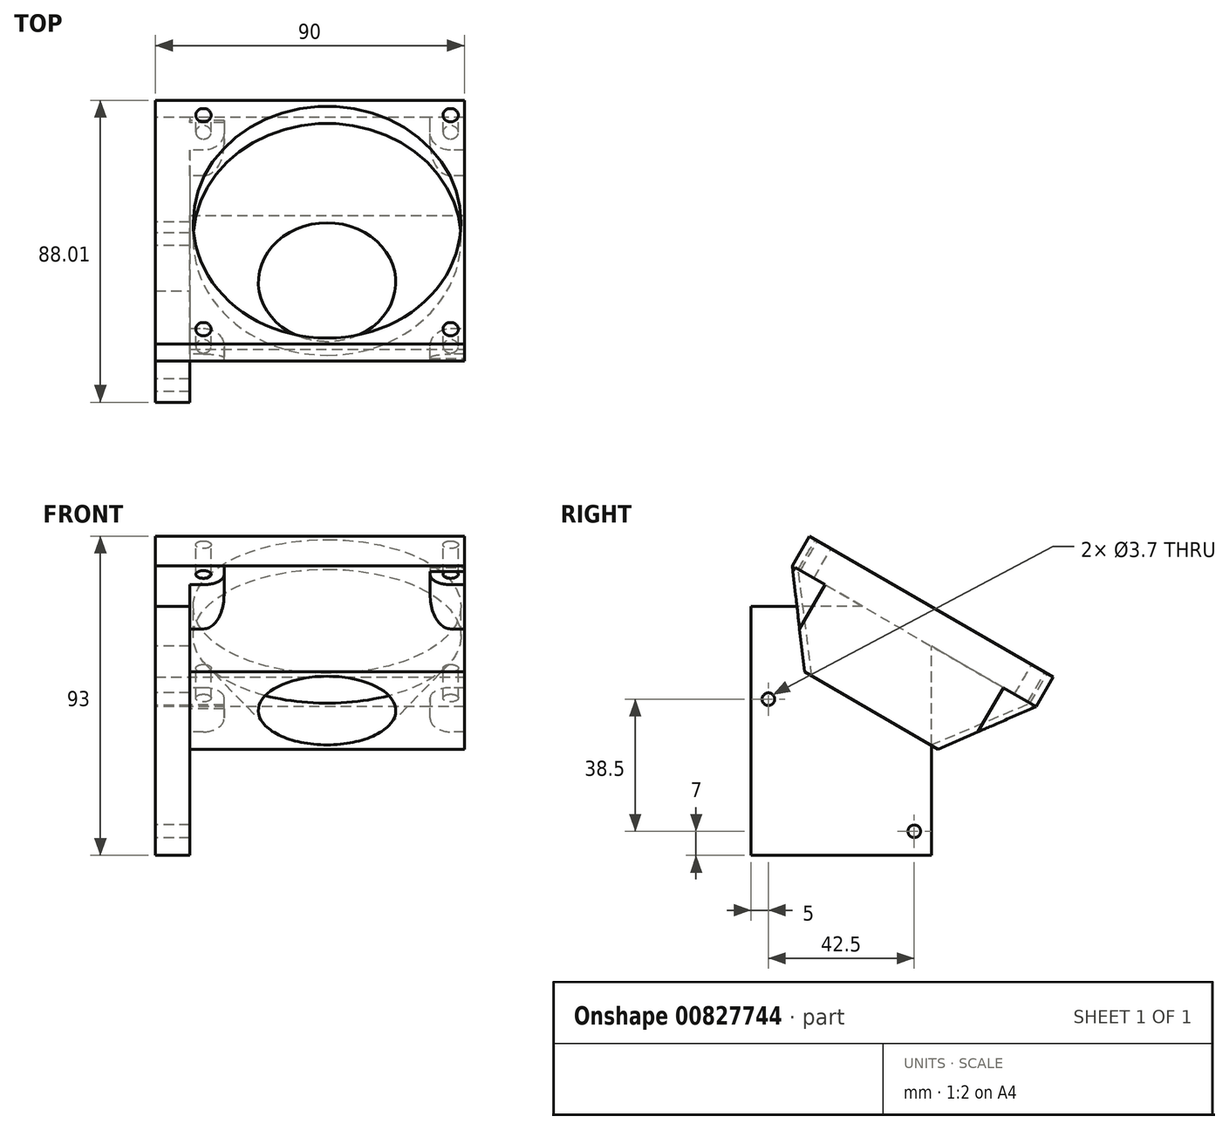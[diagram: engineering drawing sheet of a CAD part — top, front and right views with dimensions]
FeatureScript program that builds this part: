
annotation { "Feature Type Name" : "Feature", "Feature Type Description" : "" }
export const myFeature = defineFeature(function(context is Context, id is Id, definition is map)
    precondition{}
    {
        {
            var Q0;
            Q0=qCreatedBy(makeId("Right.planeOp"),FACE);
            var sketch = newSketch(context, id + "F0", { "sketchPlane" : qUnion([Q0])});
            skCircle(sketch, "E0", {"center": v(21.25, 7) * mm, "radius": 1.85 * mm});
            skCircle(sketch, "E1", {"center": v(-21.25, 45.5) * mm, "radius": 1.85 * mm});
            skLineSegment(sketch, "E2", {"start": v(26.25, 0) * mm, "end": v(-26.25, 0) * mm});
            skLineSegment(sketch, "E3", {"start": v(-26.25, 72.5) * mm, "end": v(-26.25, 0) * mm});
            skLineSegment(sketch, "E4", {"start": v(26.25, 0) * mm, "end": v(26.25, 72.5) * mm});
            skLineSegment(sketch, "E5", {"start": v(26.25, 72.5) * mm, "end": v(-26.25, 72.5) * mm});
            skLineSegment(sketch, "E6", {"start": v(0, -20.83) * mm, "end": v(0, 71.54) * mm, "construction": true});
            skLineSegment(sketch, "E7", {"start": v(-21.25, 45.5) * mm, "end": v(-21.25, 71.19) * mm, "construction": true});
            skLineSegment(sketch, "E8", {"start": v(21.25, 7) * mm, "end": v(21.25, 71.54) * mm, "construction": true});
            skSolve(sketch);
        }
        {
            var Q0;
            Q0=qSketchRegion(id+"F0",true);
            extrude(context, id + "F1", {"entities" : qUnion([Q0]), "depth" : 10 * mm, "offsetDistance" : 25 * mm});
        }
        {
            var Q0;
            Q0=qCreatedBy(makeId("Front.planeOp"),FACE);
            var Q1;
            Q1=makeQuery(id+"F1.opExtrude","SWEPT_EDGE",EDGE,{"disambiguationData":[OSD([sQuery(id+"F0.wireOp",EDGE,"E4"),sQuery(id+"F0.wireOp",EDGE,"E5")])]});
            cPlane(context, id + "F2", {"entities" : qUnion([Q0, Q1]), "cplaneType" : CPlaneType.LINE_ANGLE, "offset" : 25 * mm, "angle" : 30 * degree, "width" : 150 * mm, "height" : 150 * mm});
        }
        {
            var Q0;
            Q0=qCreatedBy(id+"F2.planeOp",FACE);
            var sketch = newSketch(context, id + "F3", { "sketchPlane" : qUnion([Q0])});
            skLineSegment(sketch, "E9", {"start": v(-90, 75.91) * mm, "end": v(-90, 65.91) * mm});
            skLineSegment(sketch, "E10", {"start": v(-90, 65.91) * mm, "end": v(0, 65.91) * mm});
            skLineSegment(sketch, "E11", {"start": v(0, 65.91) * mm, "end": v(0, 75.91) * mm});
            skLineSegment(sketch, "E12", {"start": v(0, 75.91) * mm, "end": v(-90, 75.91) * mm});
            skSolve(sketch);
        }
        {
            var Q0;
            Q0=qSketchRegion(id+"F3",true);
            extrude(context, id + "F4", {"entities" : qUnion([Q0]), "operationType" : NewBodyOperationType.ADD, "endBound" : BoundingType.SYMMETRIC, "depth" : 82 * mm, "offsetDistance" : 25 * mm});
        }
        {
            var Q0;
            Q0=makeQuery(id+"F4.opExtrude","SWEPT_FACE",FACE,{"disambiguationData":[OSD([sQuery(id+"F3.wireOp",EDGE,"E12")])]});
            var sketch = newSketch(context, id + "F5", { "sketchPlane" : qUnion([Q0])});
            skLineSegment(sketch, "E13.bottom", {"start": v(86, -49.52) * mm, "end": v(14, -49.52) * mm, "construction": true});
            skLineSegment(sketch, "E13.top", {"start": v(86, 22.48) * mm, "end": v(14, 22.48) * mm, "construction": true});
            skLineSegment(sketch, "E13.left", {"start": v(86, -49.52) * mm, "end": v(86, 22.48) * mm, "construction": true});
            skLineSegment(sketch, "E13.right", {"start": v(14, -49.52) * mm, "end": v(14, 22.48) * mm, "construction": true});
            skPoint(sketch, "E13.middle", {"position": v(50, -13.52) * mm});
            skCircle(sketch, "E14", {"center": v(14, -49.52) * mm, "radius": 2.25 * mm});
            skCircle(sketch, "E15", {"center": v(86, -49.52) * mm, "radius": 2.25 * mm});
            skCircle(sketch, "E16", {"center": v(86, 22.48) * mm, "radius": 2.25 * mm});
            skCircle(sketch, "E17", {"center": v(14, 22.48) * mm, "radius": 2.25 * mm});
            skCircle(sketch, "E18", {"center": v(50, -13.52) * mm, "radius": 39 * mm});
            skLineSegment(sketch, "E19", {"start": v(0, -13.52) * mm, "end": v(90, -13.52) * mm, "construction": true});
            skLineSegment(sketch, "E20", {"start": v(50, -13.52) * mm, "end": v(50, -90.47) * mm, "construction": true});
            skSolve(sketch);
        }
        {
            var Q0;
            Q0=makeQuery(id+"F4.opExtrude","SWEPT_FACE",FACE,{"disambiguationData":[OSD([sQuery(id+"F3.wireOp",EDGE,"E10")])]});
            cPlane(context, id + "F6", {"entities" : qUnion([Q0]), "cplaneType" : CPlaneType.OFFSET, "offset" : 25 * mm, "width" : 150 * mm, "height" : 150 * mm});
        }
        {
            var Q0;
            Q0=qSketchRegion(id+"F5",true);
            extrude(context, id + "F7", {"entities" : qUnion([Q0]), "operationType" : NewBodyOperationType.REMOVE, "endBound" : BoundingType.THROUGH_ALL, "oppositeDirection" : true, "depth" : 25 * mm, "offsetDistance" : 25 * mm});
        }
        {
            var Q0;
            Q0=qCreatedBy(id+"F6.planeOp",FACE);
            var sketch = newSketch(context, id + "F8", { "sketchPlane" : qUnion([Q0])});
            skPoint(sketch, "E21", {"position": v(50, 13.52) * mm});
            skLineSegment(sketch, "E22.bottom", {"start": v(10, 36.02) * mm, "end": v(90, 36.02) * mm});
            skLineSegment(sketch, "E22.top", {"start": v(10, -8.98) * mm, "end": v(90, -8.98) * mm});
            skLineSegment(sketch, "E22.left", {"start": v(10, 36.02) * mm, "end": v(10, -8.98) * mm});
            skLineSegment(sketch, "E22.right", {"start": v(90, 36.02) * mm, "end": v(90, -8.98) * mm});
            skLineSegment(sketch, "E23", {"start": v(50, 13.52) * mm, "end": v(-9.33, 13.52) * mm, "construction": true});
            skSolve(sketch);
        }
        {
            var Q0;
            Q0=makeQuery(id+"F4.opExtrude","SWEPT_FACE",FACE,{"disambiguationData":[OSD([sQuery(id+"F3.wireOp",EDGE,"E10")])]});
            var sketch = newSketch(context, id + "F9", { "sketchPlane" : qUnion([Q0])});
            skLineSegment(sketch, "E24.0", {"start": v(90, 54.52) * mm, "end": v(10, 54.52) * mm});
            skLineSegment(sketch, "E24.1", {"start": v(90, -27.48) * mm, "end": v(90, 54.52) * mm});
            skLineSegment(sketch, "E24.2", {"start": v(90, -27.48) * mm, "end": v(10, -27.48) * mm});
            skLineSegment(sketch, "E25", {"start": v(10, -27.48) * mm, "end": v(10, 54.52) * mm});
            skSolve(sketch);
        }
        {
            var Q1;
            Q1 = qSketchRegion(id + "F9", true);
            var Q2;
            Q2 = qSketchRegion(id + "F8", true);
            var Q3;
            Q3=sQuery(id+"F9.wireOp",VERTEX,"E24.0.end");
            var Q4;
            Q4=sQuery(id+"F8.wireOp",VERTEX,"E22.bottom.start");
            loft(context, id + "F10", {"operationType" : NewBodyOperationType.ADD, "sheetProfilesArray" : [{ "sheetProfileEntities" : qUnion([Q1]) }, { "sheetProfileEntities" : qUnion([Q2]) }], "matchConnections" : true, "connections" : [{ "connectionEntities" : qUnion([Q3, Q4]), "connectionEdgeQueries" : qUnion([]), "connectionEdgeParameters" : [] }]});
        }
        {
            var Q0;
            Q0=makeQuery(id+"F9.imprint","IMPRINT",FACE,{"disambiguationData":[TD([[makeQuery(id+"F9.imprint","IMPRINT",EDGE,{"derivedFrom":makeQuery(id+"F7.boolean.opBoolean","INTERSECT",EDGE,{"derivedFrom":[makeQuery(id+"F4.opExtrude","SWEPT_FACE",FACE,{"disambiguationData":[OSD([sQuery(id+"F3.wireOp",EDGE,"E10")])]}),makeQuery(id+"F7.opExtrude","SWEPT_FACE",FACE,{"disambiguationData":[OSD([sQuery(id+"F5.wireOp",EDGE,"E18")])]})]})}),1.0]])]});
            var sketch = newSketch(context, id + "F11", { "sketchPlane" : qUnion([Q0])});
            skCircle(sketch, "E26.0", {"center": v(50, 13.52) * mm, "radius": 39 * mm});
            skSolve(sketch);
        }
        {
            var Q0;
            Q0=makeQuery(id+"F10.opLoft","CAP_FACE",FACE,{"disambiguationData":[OSD([makeQuery(id+"F8.imprint","IMPRINT",FACE,{"disambiguationData":[TD([[makeQuery(id+"F8.imprint","IMPRINT",EDGE,{"derivedFrom":sQuery(id+"F8.wireOp",EDGE,"E22.bottom")}),-1.0]])]})])],"isStart":true});
            var sketch = newSketch(context, id + "F12", { "sketchPlane" : qUnion([Q0])});
            skCircle(sketch, "E27", {"center": v(50, 13.52) * mm, "radius": 20 * mm});
            skSolve(sketch);
        }
        {
            var Q1;
            Q1 = qSketchRegion(id + "F11", true);
            var Q2;
            Q2 = qSketchRegion(id + "F12", true);
            loft(context, id + "F13", {"operationType" : NewBodyOperationType.REMOVE, "sheetProfilesArray" : [{ "sheetProfileEntities" : qUnion([Q1]) }, { "sheetProfileEntities" : qUnion([Q2]) }]});
        }
        {
            var Q0;
            Q0=makeQuery(id+"F4.opExtrude","SWEPT_FACE",FACE,{"disambiguationData":[OSD([sQuery(id+"F3.wireOp",EDGE,"E10")])]});
            var sketch = newSketch(context, id + "F14", { "sketchPlane" : qUnion([Q0])});
            skArc(sketch, "E28", {"start": v(14, 43.52) * mm, "mid": v(18.24, 45.27) * mm, "end": v(20, 49.52) * mm});
            skLineSegment(sketch, "E29", {"start": v(20, 49.52) * mm, "end": v(20, 54.52) * mm});
            skLineSegment(sketch, "E30", {"start": v(10, 43.52) * mm, "end": v(14, 43.52) * mm});
            skLineSegment(sketch, "E31", {"start": v(10, 43.52) * mm, "end": v(10, 54.52) * mm});
            skLineSegment(sketch, "E32", {"start": v(10, 54.52) * mm, "end": v(20, 54.52) * mm});
            skLineSegment(sketch, "E33.1.0", {"start": v(20, -26.48) * mm, "end": v(9, -26.48) * mm});
            skLineSegment(sketch, "E33.1.1", {"start": v(14, -16.48) * mm, "end": v(9, -16.48) * mm});
            skLineSegment(sketch, "E33.1.2", {"start": v(20, -26.48) * mm, "end": v(20, -22.48) * mm});
            skArc(sketch, "E33.1.3", {"start": v(20, -22.48) * mm, "mid": v(18.24, -18.24) * mm, "end": v(14, -16.48) * mm});
            skLineSegment(sketch, "E33.1.4", {"start": v(9, -26.48) * mm, "end": v(9, -16.48) * mm});
            skLineSegment(sketch, "E33.2.0", {"start": v(90, -16.48) * mm, "end": v(90, -27.48) * mm});
            skLineSegment(sketch, "E33.2.1", {"start": v(80, -22.48) * mm, "end": v(80, -27.48) * mm});
            skLineSegment(sketch, "E33.2.2", {"start": v(90, -16.48) * mm, "end": v(86, -16.48) * mm});
            skArc(sketch, "E33.2.3", {"start": v(86, -16.48) * mm, "mid": v(81.76, -18.24) * mm, "end": v(80, -22.48) * mm});
            skLineSegment(sketch, "E33.2.4", {"start": v(90, -27.48) * mm, "end": v(80, -27.48) * mm});
            skLineSegment(sketch, "E33.3.0", {"start": v(80, 53.52) * mm, "end": v(91, 53.52) * mm});
            skLineSegment(sketch, "E33.3.1", {"start": v(86, 43.52) * mm, "end": v(91, 43.52) * mm});
            skLineSegment(sketch, "E33.3.2", {"start": v(80, 53.52) * mm, "end": v(80, 49.52) * mm});
            skArc(sketch, "E33.3.3", {"start": v(80, 49.52) * mm, "mid": v(81.76, 45.27) * mm, "end": v(86, 43.52) * mm});
            skLineSegment(sketch, "E33.3.4", {"start": v(91, 53.52) * mm, "end": v(91, 43.52) * mm});
            skPoint(sketch, "E33.center", {"position": v(50, 13.52) * mm});
            skSolve(sketch);
        }
        {
            var Q0;
            Q0=qSketchRegion(id+"F14",true);
            var Q1;
            Q1=makeQuery(id+"F10.opLoft","CAP_FACE",FACE,{"disambiguationData":[OSD([makeQuery(id+"F8.imprint","IMPRINT",FACE,{"disambiguationData":[TD([[makeQuery(id+"F8.imprint","IMPRINT",EDGE,{"derivedFrom":sQuery(id+"F8.wireOp",EDGE,"E22.bottom")}),-1.0]])]})])],"isStart":true});
            extrude(context, id + "F15", {"entities" : qUnion([Q0]), "operationType" : NewBodyOperationType.REMOVE, "endBound" : BoundingType.UP_TO_SURFACE, "depth" : 25 * mm, "endBoundEntityFace" : qUnion([Q1]), "offsetDistance" : 25 * mm});
        }
    });
